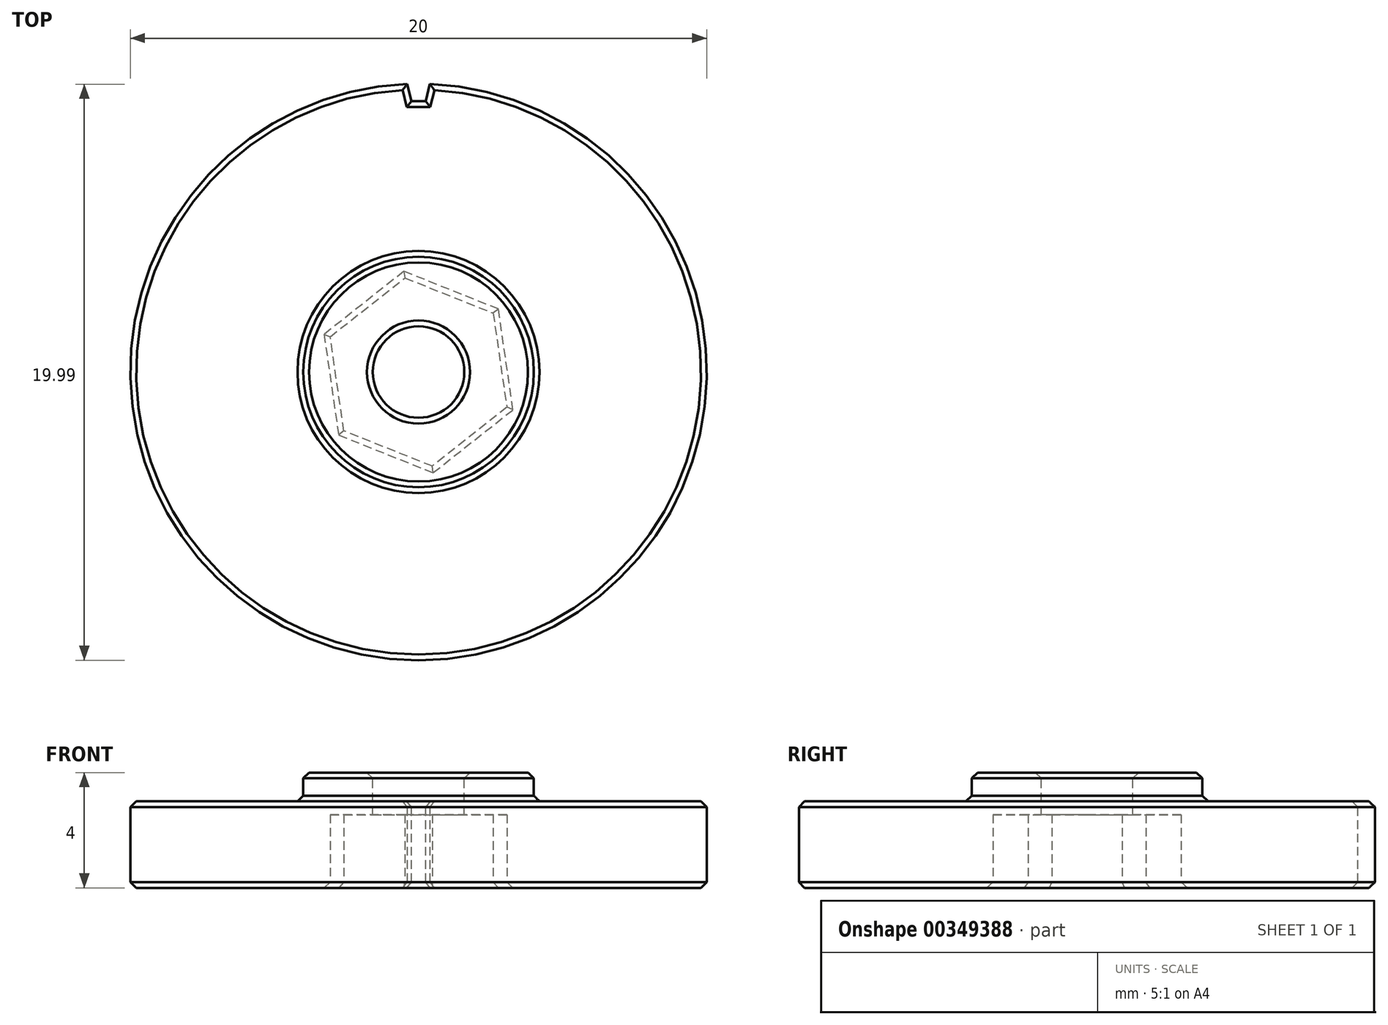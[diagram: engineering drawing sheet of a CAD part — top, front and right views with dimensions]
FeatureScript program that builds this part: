
annotation { "Feature Type Name" : "Feature", "Feature Type Description" : "" }
export const myFeature = defineFeature(function(context is Context, id is Id, definition is map)
    precondition{}
    {
        {
            var Q0;
            Q0=qCreatedBy(makeId("Top.planeOp"),FACE);
            var sketch = newSketch(context, id + "F0", { "sketchPlane" : qUnion([Q0])});
            skCircle(sketch, "E0", {"center": v(0, 0) * mm, "radius": 10 * mm});
            skSolve(sketch);
        }
        {
            var Q0;
            Q0 = qSketchRegion(id + "F0", true);
            extrude(context, id + "F1", {"entities" : qUnion([Q0]), "depth" : 3 * mm});
        }
        {
            var Q0;
            Q0=makeQuery(id+"F1.opExtrude","CAP_FACE",FACE,{"disambiguationData":[OSD([sQuery(id+"F0.wireOp",EDGE,"E0")])],"isStart":false});
            var sketch = newSketch(context, id + "F2", { "sketchPlane" : qUnion([Q0])});
            skCircle(sketch, "E1", {"center": v(0, 0) * mm, "radius": 4 * mm});
            skSolve(sketch);
        }
        {
            var Q0;
            Q0 = qSketchRegion(id + "F2", true);
            extrude(context, id + "F3", {"entities" : qUnion([Q0]), "operationType" : NewBodyOperationType.ADD, "depth" : 1 * mm});
        }
        {
            var Q0;
            Q0=makeQuery(id+"F1.opExtrude","CAP_FACE",FACE,{"disambiguationData":[OSD([sQuery(id+"F0.wireOp",EDGE,"E0")])],"isStart":true});
            var sketch = newSketch(context, id + "F4", { "sketchPlane" : qUnion([Q0])});
            skCircle(sketch, "E2.cCircle", {"center": v(0, 0) * mm, "radius": 2.86 * mm, "construction": true});
            skLineSegment(sketch, "E2.0", {"start": v(-0.47, -3.27) * mm, "end": v(-3.06, -1.22) * mm});
            skLineSegment(sketch, "E2.1", {"start": v(-3.06, -1.22) * mm, "end": v(-2.6, 2.04) * mm});
            skLineSegment(sketch, "E2.2", {"start": v(-2.6, 2.04) * mm, "end": v(0.47, 3.27) * mm});
            skLineSegment(sketch, "E2.3", {"start": v(0.47, 3.27) * mm, "end": v(3.06, 1.22) * mm});
            skLineSegment(sketch, "E2.4", {"start": v(3.06, 1.22) * mm, "end": v(2.6, -2.04) * mm});
            skLineSegment(sketch, "E2.5", {"start": v(2.6, -2.04) * mm, "end": v(-0.47, -3.27) * mm});
            skPoint(sketch, "E2.0.midPoint", {"position": v(-1.77, -2.24) * mm});
            skSolve(sketch);
        }
        {
            var Q0;
            Q0 = qSketchRegion(id + "F4", true);
            extrude(context, id + "F5", {"entities" : qUnion([Q0]), "operationType" : NewBodyOperationType.REMOVE, "oppositeDirection" : true, "depth" : 2.54 * mm});
        }
        {
            var Q0;
            Q0=makeQuery(id+"F1.opExtrude","CAP_FACE",FACE,{"disambiguationData":[OSD([sQuery(id+"F0.wireOp",EDGE,"E0")])],"isStart":false});
            var sketch = newSketch(context, id + "F6", { "sketchPlane" : qUnion([Q0])});
            skLineSegment(sketch, "E3", {"start": v(-0.5, 10.41) * mm, "end": v(-0.25, 9.4) * mm});
            skLineSegment(sketch, "E4", {"start": v(-0.25, 9.4) * mm, "end": v(0.25, 9.4) * mm});
            skLineSegment(sketch, "E5", {"start": v(0.25, 9.4) * mm, "end": v(0.5, 10.41) * mm});
            skLineSegment(sketch, "E6", {"start": v(0.5, 10.41) * mm, "end": v(-0.5, 10.41) * mm});
            skLineSegment(sketch, "E7", {"start": v(0, 0) * mm, "end": v(0, 14.54) * mm, "construction": true});
            skSolve(sketch);
        }
        {
            var Q0;
            Q0 = qSketchRegion(id + "F6", true);
            extrude(context, id + "F7", {"entities" : qUnion([Q0]), "operationType" : NewBodyOperationType.REMOVE, "endBound" : BoundingType.THROUGH_ALL, "oppositeDirection" : true, "depth" : 25.4 * mm});
        }
        {
            var Q0;
            Q0=makeQuery(id+"F3.opExtrude","CAP_FACE",FACE,{"disambiguationData":[OSD([sQuery(id+"F2.wireOp",EDGE,"E1")])],"isStart":false});
            var sketch = newSketch(context, id + "F8", { "sketchPlane" : qUnion([Q0])});
            skCircle(sketch, "E8", {"center": v(0, 0) * mm, "radius": 1.59 * mm});
            skSolve(sketch);
        }
        {
            var Q0;
            Q0 = qSketchRegion(id + "F8", true);
            extrude(context, id + "F9", {"entities" : qUnion([Q0]), "operationType" : NewBodyOperationType.REMOVE, "endBound" : BoundingType.THROUGH_ALL, "oppositeDirection" : true, "depth" : 25.4 * mm});
        }
        {
            var Q0;
            Q0=makeQuery(id+"F1.opExtrude","CAP_FACE",FACE,{"disambiguationData":[OSD([sQuery(id+"F0.wireOp",EDGE,"E0")])],"isStart":true});
            var Q1;
            Q1=makeQuery(id+"F1.opExtrude","CAP_FACE",FACE,{"disambiguationData":[OSD([sQuery(id+"F0.wireOp",EDGE,"E0")])],"isStart":false});
            var Q2;
            Q2=makeQuery(id+"F3.opExtrude","CAP_FACE",FACE,{"disambiguationData":[OSD([sQuery(id+"F2.wireOp",EDGE,"E1")])],"isStart":false});
            chamfer(context, id + "F10", {"entities" : qUnion([Q0, Q1, Q2]), "width" : .2 * mm, "tangentPropagation" : true});
        }
    });
